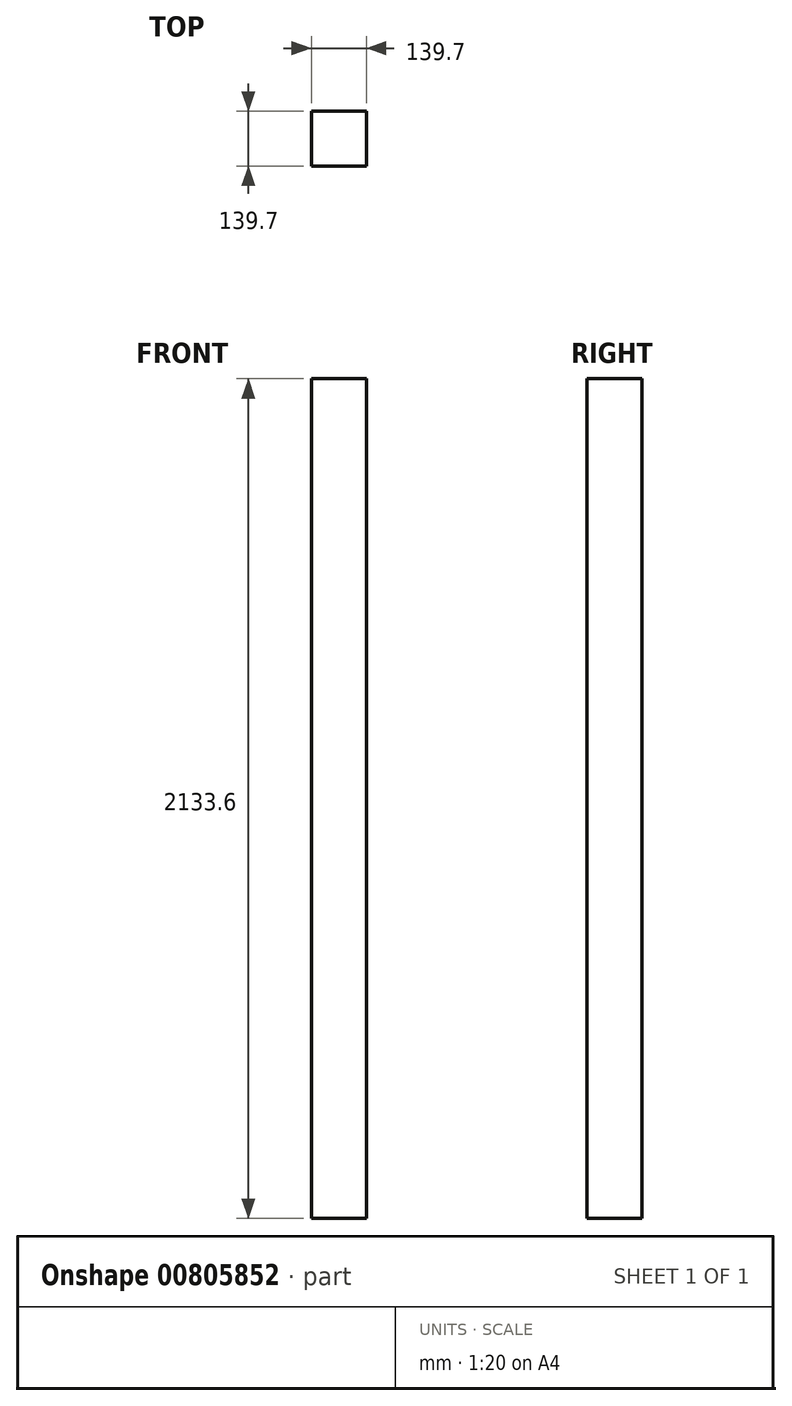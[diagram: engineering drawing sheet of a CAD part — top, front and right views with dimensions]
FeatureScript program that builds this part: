
annotation { "Feature Type Name" : "Feature", "Feature Type Description" : "" }
export const myFeature = defineFeature(function(context is Context, id is Id, definition is map)
    precondition{}
    {
        {
            var Q0;
            Q0=qCreatedBy(makeId("Top.planeOp"),FACE);
            var sketch = newSketch(context, id + "F0", { "sketchPlane" : qUnion([Q0])});
            skLineSegment(sketch, "E0.bottom", {"start": v(-69.85, 69.85) * mm, "end": v(69.85, 69.85) * mm});
            skLineSegment(sketch, "E0.top", {"start": v(-69.85, -69.85) * mm, "end": v(69.85, -69.85) * mm});
            skLineSegment(sketch, "E0.left", {"start": v(-69.85, 69.85) * mm, "end": v(-69.85, -69.85) * mm});
            skLineSegment(sketch, "E0.right", {"start": v(69.85, 69.85) * mm, "end": v(69.85, -69.85) * mm});
            skSolve(sketch);
        }
        {
            var Q0;
            Q0=makeQuery(id+"F0.imprint","IMPRINT",FACE,{"disambiguationData":[TD([[makeQuery(id+"F0.imprint","IMPRINT",EDGE,{"derivedFrom":sQuery(id+"F0.wireOp",EDGE,"E0.bottom")}),-1.0]])]});
            extrude(context, id + "F1", {"entities" : qUnion([Q0]), "depth" : 2133.6 * mm, "offsetDistance" : 25.4 * mm});
        }
    });
